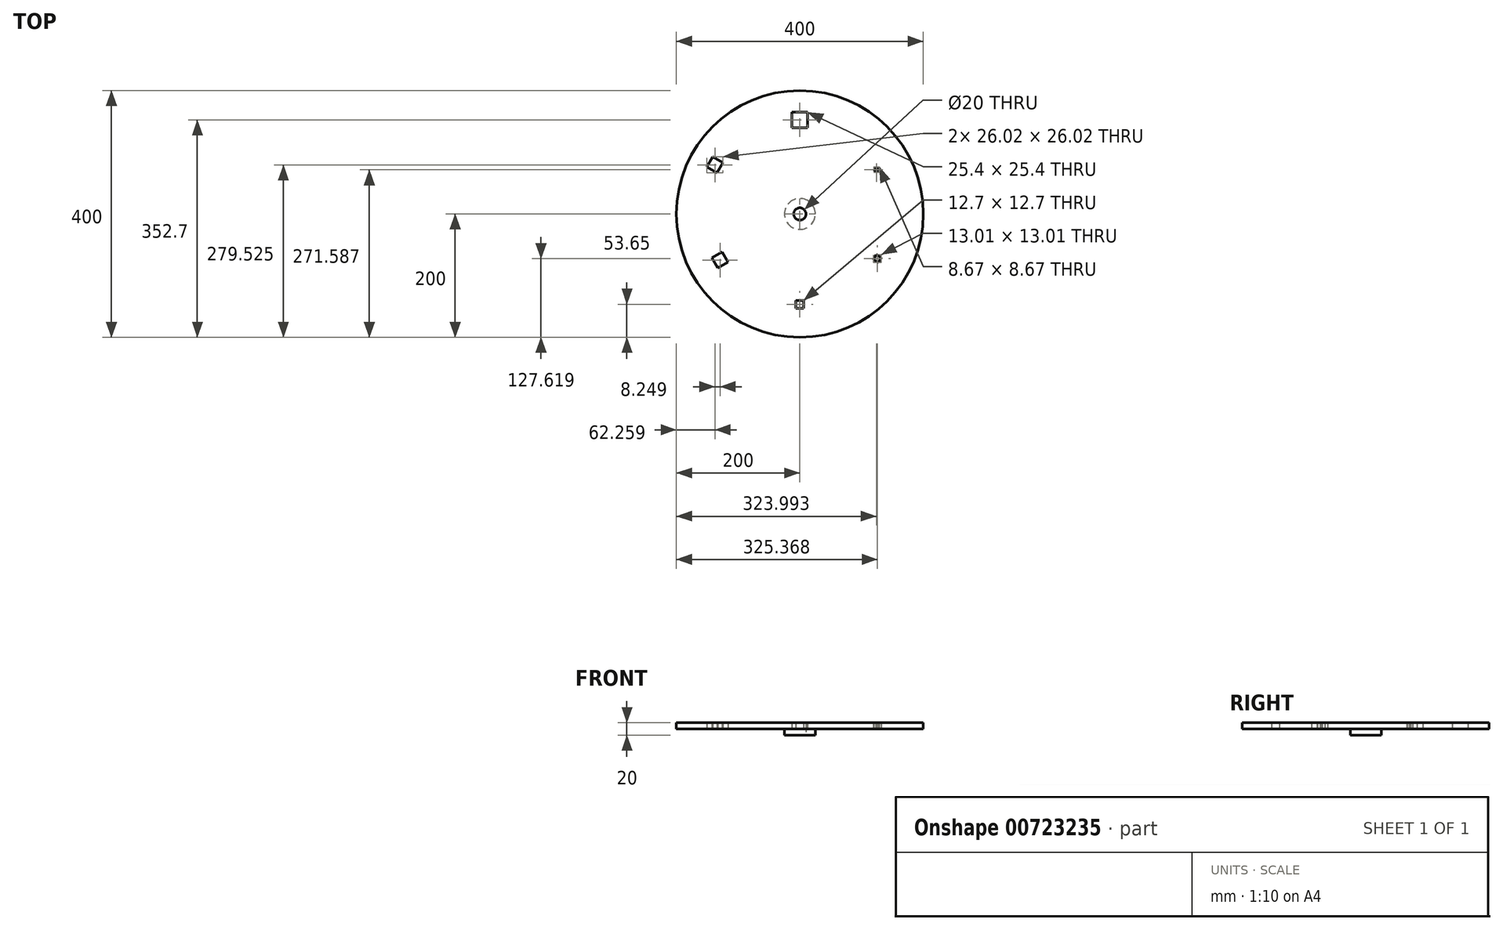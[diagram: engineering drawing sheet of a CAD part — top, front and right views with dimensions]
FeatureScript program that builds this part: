
annotation { "Feature Type Name" : "Feature", "Feature Type Description" : "" }
export const myFeature = defineFeature(function(context is Context, id is Id, definition is map)
    precondition{}
    {
        {
            var Q0;
            Q0=qCreatedBy(makeId("Top.planeOp"),FACE);
            var sketch = newSketch(context, id + "F0", { "sketchPlane" : qUnion([Q0])});
            skCircle(sketch, "E0", {"center": v(0, 0) * mm, "radius": 200 * mm});
            skCircle(sketch, "E1", {"center": v(0, 0) * mm, "radius": 10 * mm});
            skLineSegment(sketch, "E2.bottom", {"start": v(-12.7, 165.4) * mm, "end": v(12.7, 165.4) * mm});
            skLineSegment(sketch, "E2.top", {"start": v(-12.7, 140) * mm, "end": v(12.7, 140) * mm});
            skLineSegment(sketch, "E2.left", {"start": v(-12.7, 165.4) * mm, "end": v(-12.7, 140) * mm});
            skLineSegment(sketch, "E2.right", {"start": v(12.7, 165.4) * mm, "end": v(12.7, 140) * mm});
            skLineSegment(sketch, "E3.bottom", {"start": v(-6.35, -140) * mm, "end": v(6.35, -140) * mm});
            skLineSegment(sketch, "E3.top", {"start": v(-6.35, -152.7) * mm, "end": v(6.35, -152.7) * mm});
            skLineSegment(sketch, "E3.left", {"start": v(-6.35, -140) * mm, "end": v(-6.35, -152.7) * mm});
            skLineSegment(sketch, "E3.right", {"start": v(6.35, -140) * mm, "end": v(6.35, -152.7) * mm});
            skLineSegment(sketch, "E4.bottom", {"start": v(-150.75, 76.04) * mm, "end": v(-141.23, 92.54) * mm});
            skLineSegment(sketch, "E4.top", {"start": v(-134.25, 66.51) * mm, "end": v(-124.73, 83.01) * mm});
            skLineSegment(sketch, "E4.left", {"start": v(-150.75, 76.04) * mm, "end": v(-134.25, 66.51) * mm});
            skLineSegment(sketch, "E4.right", {"start": v(-141.23, 92.54) * mm, "end": v(-124.73, 83.01) * mm});
            skLineSegment(sketch, "E5", {"start": v(0, 0) * mm, "end": v(-131.7, 76.04) * mm, "construction": true});
            skLineSegment(sketch, "E6", {"start": v(0, 0) * mm, "end": v(0, 99.53) * mm, "construction": true});
            skLineSegment(sketch, "E7", {"start": v(0, 0) * mm, "end": v(-149.62, -86.39) * mm, "construction": true});
            skLineSegment(sketch, "E8.bottom", {"start": v(-142.5, -71.28) * mm, "end": v(-126, -61.75) * mm});
            skLineSegment(sketch, "E8.top", {"start": v(-132.98, -87.77) * mm, "end": v(-116.48, -78.25) * mm});
            skLineSegment(sketch, "E8.left", {"start": v(-142.5, -71.28) * mm, "end": v(-132.98, -87.77) * mm});
            skLineSegment(sketch, "E8.right", {"start": v(-126, -61.75) * mm, "end": v(-116.48, -78.25) * mm});
            skLineSegment(sketch, "E9.bottom", {"start": v(123.62, -65.88) * mm, "end": v(131.87, -70.64) * mm});
            skLineSegment(sketch, "E9.top", {"start": v(118.86, -74.12) * mm, "end": v(127.11, -78.89) * mm});
            skLineSegment(sketch, "E9.left", {"start": v(123.62, -65.88) * mm, "end": v(118.86, -74.12) * mm});
            skLineSegment(sketch, "E9.right", {"start": v(131.87, -70.64) * mm, "end": v(127.11, -78.89) * mm});
            skLineSegment(sketch, "E10.bottom", {"start": v(119.66, 72.75) * mm, "end": v(125.16, 75.92) * mm});
            skLineSegment(sketch, "E10.top", {"start": v(122.83, 67.25) * mm, "end": v(128.33, 70.43) * mm});
            skLineSegment(sketch, "E10.left", {"start": v(119.66, 72.75) * mm, "end": v(122.83, 67.25) * mm});
            skLineSegment(sketch, "E10.right", {"start": v(125.16, 75.92) * mm, "end": v(128.33, 70.43) * mm});
            skSolve(sketch);
        }
        {
            var Q0;
            Q0 = qSketchRegion(id + "F0", true);
            extrude(context, id + "F1", {"entities" : qUnion([Q0]), "depth" : 10 * mm, "offsetDistance" : 25 * mm});
        }
        {
            var Q0;
            Q0=makeQuery(id+"F1.opExtrude","CAP_FACE",FACE,{"disambiguationData":[OSD([sQuery(id+"F0.wireOp",EDGE,"E0"),sQuery(id+"F0.wireOp",EDGE,"E1"),sQuery(id+"F0.wireOp",EDGE,"E2.bottom"),sQuery(id+"F0.wireOp",EDGE,"E2.top"),sQuery(id+"F0.wireOp",EDGE,"E2.left"),sQuery(id+"F0.wireOp",EDGE,"E2.right")])],"isStart":true});
            var sketch = newSketch(context, id + "F2", { "sketchPlane" : qUnion([Q0])});
            skCircle(sketch, "E11", {"center": v(0, 0) * mm, "radius": 25 * mm});
            skCircle(sketch, "E12", {"center": v(0, 0) * mm, "radius": 10 * mm});
            skSolve(sketch);
        }
        {
            var Q0;
            Q0 = qSketchRegion(id + "F2", true);
            extrude(context, id + "F3", {"entities" : qUnion([Q0]), "operationType" : NewBodyOperationType.ADD, "depth" : 10 * mm, "offsetDistance" : 25 * mm});
        }
    });
